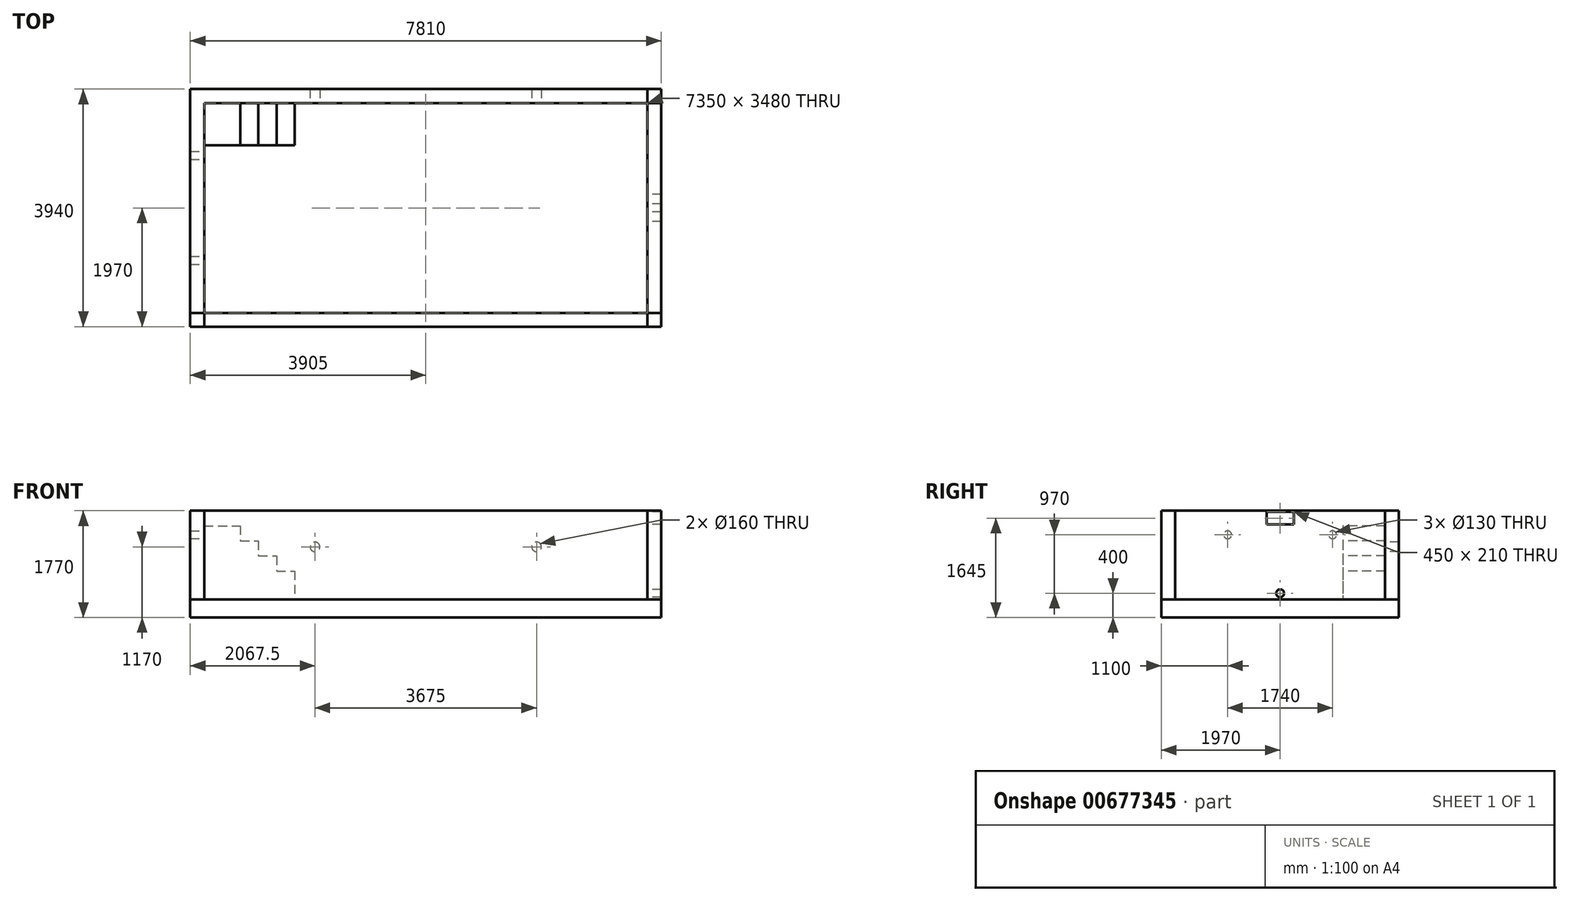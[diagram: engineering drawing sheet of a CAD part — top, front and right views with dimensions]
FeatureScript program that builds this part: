
annotation { "Feature Type Name" : "Feature", "Feature Type Description" : "" }
export const myFeature = defineFeature(function(context is Context, id is Id, definition is map)
    precondition{}
    {
        {
            var Q0;
            Q0=qCreatedBy(makeId("Top.planeOp"),FACE);
            var sketch = newSketch(context, id + "F0", { "sketchPlane" : qUnion([Q0])});
            skLineSegment(sketch, "E0.bottom", {"start": v(-3905, -1970) * mm, "end": v(3905, -1970) * mm});
            skLineSegment(sketch, "E0.top", {"start": v(-3905, 1970) * mm, "end": v(3905, 1970) * mm});
            skLineSegment(sketch, "E0.left", {"start": v(-3905, -1970) * mm, "end": v(-3905, 1970) * mm});
            skLineSegment(sketch, "E0.right", {"start": v(3905, -1970) * mm, "end": v(3905, 1970) * mm});
            skPoint(sketch, "E0.middle", {"position": v(0, 0) * mm});
            skSolve(sketch);
        }
        {
            var Q0;
            Q0=qSketchRegion(id+"F0",true);
            extrude(context, id + "F1", {"entities" : qUnion([Q0]), "oppositeDirection" : true, "depth" : 300 * mm});
        }
        {
            var Q0;
            Q0=makeQuery(id+"F1.opExtrude","CAP_FACE",FACE,{"disambiguationData":[OSD([sQuery(id+"F0.wireOp",EDGE,"E0.bottom"),sQuery(id+"F0.wireOp",EDGE,"E0.top"),sQuery(id+"F0.wireOp",EDGE,"E0.left"),sQuery(id+"F0.wireOp",EDGE,"E0.right")])],"isStart":true});
            var sketch = newSketch(context, id + "F2", { "sketchPlane" : qUnion([Q0])});
            skLineSegment(sketch, "E1.bottom", {"start": v(-3905, 1970) * mm, "end": v(-3675, 1970) * mm});
            skLineSegment(sketch, "E1.top", {"start": v(-3905, -1970) * mm, "end": v(-3675, -1970) * mm});
            skLineSegment(sketch, "E1.left", {"start": v(-3905, 1970) * mm, "end": v(-3905, -1970) * mm});
            skLineSegment(sketch, "E1.right", {"start": v(-3675, 1970) * mm, "end": v(-3675, -1970) * mm});
            skLineSegment(sketch, "E2.bottom", {"start": v(3905, 1970) * mm, "end": v(3675, 1970) * mm});
            skLineSegment(sketch, "E2.top", {"start": v(3905, -1970) * mm, "end": v(3675, -1970) * mm});
            skLineSegment(sketch, "E2.left", {"start": v(3905, 1970) * mm, "end": v(3905, -1970) * mm});
            skLineSegment(sketch, "E2.right", {"start": v(3675, 1970) * mm, "end": v(3675, -1970) * mm});
            skLineSegment(sketch, "E3.bottom", {"start": v(-3675, 1970) * mm, "end": v(3675, 1970) * mm});
            skLineSegment(sketch, "E3.top", {"start": v(-3675, 1740) * mm, "end": v(3675, 1740) * mm});
            skLineSegment(sketch, "E3.left", {"start": v(-3675, 1970) * mm, "end": v(-3675, 1740) * mm});
            skLineSegment(sketch, "E3.right", {"start": v(3675, 1970) * mm, "end": v(3675, 1740) * mm});
            skLineSegment(sketch, "E4.bottom", {"start": v(-3675, -1970) * mm, "end": v(3675, -1970) * mm});
            skLineSegment(sketch, "E4.top", {"start": v(-3675, -1740) * mm, "end": v(3675, -1740) * mm});
            skLineSegment(sketch, "E4.left", {"start": v(-3675, -1970) * mm, "end": v(-3675, -1740) * mm});
            skLineSegment(sketch, "E4.right", {"start": v(3675, -1970) * mm, "end": v(3675, -1740) * mm});
            skLineSegment(sketch, "E5.bottom", {"start": v(-3675, -1740) * mm, "end": v(-3905, -1740) * mm});
            skLineSegment(sketch, "E5.top", {"start": v(-3675, -1970) * mm, "end": v(-3905, -1970) * mm});
            skLineSegment(sketch, "E5.left", {"start": v(-3675, -1740) * mm, "end": v(-3675, -1970) * mm});
            skLineSegment(sketch, "E5.right", {"start": v(-3905, -1740) * mm, "end": v(-3905, -1970) * mm});
            skLineSegment(sketch, "E6.bottom", {"start": v(-3675, 1740) * mm, "end": v(-3905, 1740) * mm});
            skLineSegment(sketch, "E6.top", {"start": v(-3675, 1970) * mm, "end": v(-3905, 1970) * mm});
            skLineSegment(sketch, "E6.left", {"start": v(-3675, 1740) * mm, "end": v(-3675, 1970) * mm});
            skLineSegment(sketch, "E6.right", {"start": v(-3905, 1740) * mm, "end": v(-3905, 1970) * mm});
            skLineSegment(sketch, "E7.bottom", {"start": v(3675, 1740) * mm, "end": v(3905, 1740) * mm});
            skLineSegment(sketch, "E7.top", {"start": v(3675, 1970) * mm, "end": v(3905, 1970) * mm});
            skLineSegment(sketch, "E7.left", {"start": v(3675, 1740) * mm, "end": v(3675, 1970) * mm});
            skLineSegment(sketch, "E7.right", {"start": v(3905, 1740) * mm, "end": v(3905, 1970) * mm});
            skLineSegment(sketch, "E8.bottom", {"start": v(3675, -1740) * mm, "end": v(3905, -1740) * mm});
            skLineSegment(sketch, "E8.top", {"start": v(3675, -1970) * mm, "end": v(3905, -1970) * mm});
            skLineSegment(sketch, "E8.left", {"start": v(3675, -1740) * mm, "end": v(3675, -1970) * mm});
            skLineSegment(sketch, "E8.right", {"start": v(3905, -1740) * mm, "end": v(3905, -1970) * mm});
            skSolve(sketch);
        }
        {
            var Q0;
            Q0=makeQuery(id+"F2.imprint","IMPRINT",FACE,{"disambiguationData":[TD([[makeQuery(id+"F2.imprint","IMPRINT",EDGE,{"derivedFrom":sQuery(id+"F2.wireOp",EDGE,"E1.left")}),-1.0]])]});
            var Q1;
            Q1=makeQuery(id+"F2.imprint","IMPRINT",FACE,{"disambiguationData":[TD([[makeQuery(id+"F2.imprint","IMPRINT",EDGE,{"derivedFrom":sQuery(id+"F2.wireOp",EDGE,"E2.left")}),1.0]])]});
            var Q2;
            Q2=makeQuery(id+"F2.imprint","IMPRINT",FACE,{"disambiguationData":[TD([[makeQuery(id+"F2.imprint","IMPRINT",EDGE,{"derivedFrom":sQuery(id+"F2.wireOp",EDGE,"E3.bottom")}),-1.0]])]});
            var Q3;
            Q3=makeQuery(id+"F2.imprint","IMPRINT",FACE,{"disambiguationData":[TD([[makeQuery(id+"F2.imprint","IMPRINT",EDGE,{"derivedFrom":sQuery(id+"F2.wireOp",EDGE,"E4.bottom")}),1.0]])]});
            extrude(context, id + "F3", {"entities" : qUnion([Q0, Q1, Q2, Q3]), "depth" : 1470 * mm, "offsetDistance" : 25 * mm});
        }
        {
            var Q0;
            Q0=makeQuery(id+"F2.imprint","IMPRINT",FACE,{"disambiguationData":[TD([[makeQuery(id+"F2.imprint","IMPRINT",EDGE,{"derivedFrom":sQuery(id+"F2.wireOp",EDGE,"E5.bottom")}),1.0]])]});
            var Q1;
            Q1=makeQuery(id+"F2.imprint","IMPRINT",FACE,{"disambiguationData":[TD([[makeQuery(id+"F2.imprint","IMPRINT",EDGE,{"derivedFrom":sQuery(id+"F2.wireOp",EDGE,"E6.bottom")}),-1.0]])]});
            var Q2;
            Q2=makeQuery(id+"F2.imprint","IMPRINT",FACE,{"disambiguationData":[TD([[makeQuery(id+"F2.imprint","IMPRINT",EDGE,{"derivedFrom":sQuery(id+"F2.wireOp",EDGE,"E7.bottom")}),1.0]])]});
            var Q3;
            Q3=makeQuery(id+"F2.imprint","IMPRINT",FACE,{"disambiguationData":[TD([[makeQuery(id+"F2.imprint","IMPRINT",EDGE,{"derivedFrom":sQuery(id+"F2.wireOp",EDGE,"E8.bottom")}),-1.0]])]});
            extrude(context, id + "F4", {"entities" : qUnion([Q0, Q1, Q2, Q3]), "depth" : 1470 * mm, "offsetDistance" : 25 * mm});
        }
        {
            var Q0;
            Q0=makeQuery(id+"F1.opExtrude","CAP_FACE",FACE,{"disambiguationData":[OSD([sQuery(id+"F0.wireOp",EDGE,"E0.bottom"),sQuery(id+"F0.wireOp",EDGE,"E0.top"),sQuery(id+"F0.wireOp",EDGE,"E0.left"),sQuery(id+"F0.wireOp",EDGE,"E0.right")])],"isStart":true});
            var sketch = newSketch(context, id + "F5", { "sketchPlane" : qUnion([Q0])});
            skLineSegment(sketch, "E9.bottom", {"start": v(-3905, 1970) * mm, "end": v(-3675, 1970) * mm});
            skLineSegment(sketch, "E9.top", {"start": v(-3905, 1740) * mm, "end": v(-3675, 1740) * mm});
            skLineSegment(sketch, "E9.left", {"start": v(-3905, 1970) * mm, "end": v(-3905, 1740) * mm});
            skLineSegment(sketch, "E9.right", {"start": v(-3675, 1970) * mm, "end": v(-3675, 1740) * mm});
            skLineSegment(sketch, "E10.bottom", {"start": v(-3675, 1740) * mm, "end": v(-2175, 1740) * mm});
            skLineSegment(sketch, "E10.top", {"start": v(-3675, 1040) * mm, "end": v(-2175, 1040) * mm});
            skLineSegment(sketch, "E10.left", {"start": v(-3675, 1740) * mm, "end": v(-3675, 1040) * mm});
            skLineSegment(sketch, "E10.right", {"start": v(-2175, 1740) * mm, "end": v(-2175, 1040) * mm});
            skSolve(sketch);
        }
        {
            var Q0;
            Q0=makeQuery(id+"F5.imprint","IMPRINT",FACE,{"disambiguationData":[TD([[makeQuery(id+"F5.imprint","IMPRINT",EDGE,{"derivedFrom":sQuery(id+"F5.wireOp",EDGE,"E10.bottom")}),-1.0]])]});
            extrude(context, id + "F6", {"entities" : qUnion([Q0]), "depth" : 470 * mm, "offsetDistance" : 25 * mm});
        }
        {
            var Q0;
            Q0=makeQuery(id+"F6.opExtrude","CAP_FACE",FACE,{"disambiguationData":[OSD([sQuery(id+"F5.wireOp",EDGE,"E10.bottom"),sQuery(id+"F5.wireOp",EDGE,"E10.top"),sQuery(id+"F5.wireOp",EDGE,"E10.left"),sQuery(id+"F5.wireOp",EDGE,"E10.right")])],"isStart":false});
            var sketch = newSketch(context, id + "F7", { "sketchPlane" : qUnion([Q0])});
            skLineSegment(sketch, "E11.bottom", {"start": v(-3675, 1740) * mm, "end": v(-2475, 1740) * mm});
            skLineSegment(sketch, "E11.top", {"start": v(-3675, 1040) * mm, "end": v(-2475, 1040) * mm});
            skLineSegment(sketch, "E11.left", {"start": v(-3675, 1740) * mm, "end": v(-3675, 1040) * mm});
            skLineSegment(sketch, "E11.right", {"start": v(-2475, 1740) * mm, "end": v(-2475, 1040) * mm});
            skSolve(sketch);
        }
        {
            var Q0;
            Q0 = qSketchRegion(id + "F7", true);
            extrude(context, id + "F8", {"entities" : qUnion([Q0]), "operationType" : NewBodyOperationType.ADD, "depth" : 250 * mm, "offsetDistance" : 25 * mm});
        }
        {
            var Q0;
            Q0=makeQuery(id+"F8.opExtrude","CAP_FACE",FACE,{"disambiguationData":[OSD([sQuery(id+"F7.wireOp",EDGE,"E11.bottom"),sQuery(id+"F7.wireOp",EDGE,"E11.top"),sQuery(id+"F7.wireOp",EDGE,"E11.left"),sQuery(id+"F7.wireOp",EDGE,"E11.right")])],"isStart":false});
            var sketch = newSketch(context, id + "F9", { "sketchPlane" : qUnion([Q0])});
            skLineSegment(sketch, "E12.bottom", {"start": v(-3675, 1740) * mm, "end": v(-2775, 1740) * mm});
            skLineSegment(sketch, "E12.top", {"start": v(-3675, 1040) * mm, "end": v(-2775, 1040) * mm});
            skLineSegment(sketch, "E12.left", {"start": v(-3675, 1740) * mm, "end": v(-3675, 1040) * mm});
            skLineSegment(sketch, "E12.right", {"start": v(-2775, 1740) * mm, "end": v(-2775, 1040) * mm});
            skSolve(sketch);
        }
        {
            var Q0;
            Q0 = qSketchRegion(id + "F9", true);
            extrude(context, id + "F10", {"entities" : qUnion([Q0]), "operationType" : NewBodyOperationType.ADD, "depth" : 250 * mm, "offsetDistance" : 25 * mm});
        }
        {
            var Q0;
            Q0=makeQuery(id+"F10.opExtrude","CAP_FACE",FACE,{"disambiguationData":[OSD([sQuery(id+"F9.wireOp",EDGE,"E12.bottom"),sQuery(id+"F9.wireOp",EDGE,"E12.top"),sQuery(id+"F9.wireOp",EDGE,"E12.left"),sQuery(id+"F9.wireOp",EDGE,"E12.right")])],"isStart":false});
            var sketch = newSketch(context, id + "F11", { "sketchPlane" : qUnion([Q0])});
            skLineSegment(sketch, "E13.bottom", {"start": v(-3675, 1740) * mm, "end": v(-3075, 1740) * mm});
            skLineSegment(sketch, "E13.top", {"start": v(-3675, 1040) * mm, "end": v(-3075, 1040) * mm});
            skLineSegment(sketch, "E13.left", {"start": v(-3675, 1740) * mm, "end": v(-3675, 1040) * mm});
            skLineSegment(sketch, "E13.right", {"start": v(-3075, 1740) * mm, "end": v(-3075, 1040) * mm});
            skSolve(sketch);
        }
        {
            var Q0;
            Q0 = qSketchRegion(id + "F11", true);
            extrude(context, id + "F12", {"entities" : qUnion([Q0]), "operationType" : NewBodyOperationType.ADD, "depth" : 250 * mm, "offsetDistance" : 25 * mm});
        }
        {
            var Q0;
            Q0=makeQuery(id+"F3.opExtrude","SWEPT_FACE",FACE,{"disambiguationData":[OSD([sQuery(id+"F2.wireOp",EDGE,"E3.top")])]});
            var sketch = newSketch(context, id + "F13", { "sketchPlane" : qUnion([Q0])});
            skLineSegment(sketch, "E14.bottom", {"start": v(-3675, 1470) * mm, "end": v(-1837.5, 1470) * mm});
            skLineSegment(sketch, "E14.top", {"start": v(-3675, 870) * mm, "end": v(-1837.5, 870) * mm});
            skLineSegment(sketch, "E14.left", {"start": v(-3675, 1470) * mm, "end": v(-3675, 870) * mm});
            skLineSegment(sketch, "E14.right", {"start": v(-1837.5, 1470) * mm, "end": v(-1837.5, 870) * mm});
            skLineSegment(sketch, "E15.bottom", {"start": v(3675, 1470) * mm, "end": v(1837.5, 1470) * mm});
            skLineSegment(sketch, "E15.top", {"start": v(3675, 870) * mm, "end": v(1837.5, 870) * mm});
            skLineSegment(sketch, "E15.left", {"start": v(3675, 1470) * mm, "end": v(3675, 870) * mm});
            skLineSegment(sketch, "E15.right", {"start": v(1837.5, 1470) * mm, "end": v(1837.5, 870) * mm});
            skCircle(sketch, "E16", {"center": v(-1837.5, 870) * mm, "radius": 80 * mm});
            skCircle(sketch, "E17", {"center": v(1837.5, 870) * mm, "radius": 80 * mm});
            skSolve(sketch);
        }
        {
            var Q0;
            {var subQ0=sQuery(id+"F13.wireOp",EDGE,"E14.right");var subQ1=sQuery(id+"F13.wireOp",EDGE,"E14.top");var subQ2=makeQuery(id+"F13.imprint","INTERSECT",VERTEX,{"derivedFrom":[subQ1,subQ0]});Q0=makeQuery(id+"F13.imprint","IMPRINT",FACE,{"disambiguationData":[TD([[makeQuery(id+"F13.imprint","IMPRINT",EDGE,{"disambiguationData":[TD([[subQ2,1.0]])],"derivedFrom":subQ1}),1.0]])]});}
            var Q1;
            {var subQ0=sQuery(id+"F13.wireOp",EDGE,"E14.right");var subQ1=sQuery(id+"F13.wireOp",EDGE,"E14.top");var subQ2=makeQuery(id+"F13.imprint","INTERSECT",VERTEX,{"derivedFrom":[subQ1,subQ0]});Q1=makeQuery(id+"F13.imprint","IMPRINT",FACE,{"disambiguationData":[TD([[makeQuery(id+"F13.imprint","IMPRINT",EDGE,{"disambiguationData":[TD([[subQ2,1.0]])],"derivedFrom":subQ1}),-1.0]])]});}
            var Q2;
            {var subQ0=sQuery(id+"F13.wireOp",EDGE,"E15.right");var subQ1=sQuery(id+"F13.wireOp",EDGE,"E15.top");var subQ2=makeQuery(id+"F13.imprint","INTERSECT",VERTEX,{"derivedFrom":[subQ1,subQ0]});Q2=makeQuery(id+"F13.imprint","IMPRINT",FACE,{"disambiguationData":[TD([[makeQuery(id+"F13.imprint","IMPRINT",EDGE,{"disambiguationData":[TD([[subQ2,1.0]])],"derivedFrom":subQ1}),-1.0]])]});}
            var Q3;
            {var subQ0=sQuery(id+"F13.wireOp",EDGE,"E15.right");var subQ1=sQuery(id+"F13.wireOp",EDGE,"E15.top");var subQ2=makeQuery(id+"F13.imprint","INTERSECT",VERTEX,{"derivedFrom":[subQ1,subQ0]});Q3=makeQuery(id+"F13.imprint","IMPRINT",FACE,{"disambiguationData":[TD([[makeQuery(id+"F13.imprint","IMPRINT",EDGE,{"disambiguationData":[TD([[subQ2,1.0]])],"derivedFrom":subQ1}),1.0]])]});}
            extrude(context, id + "F14", {"entities" : qUnion([Q0, Q1, Q2, Q3]), "operationType" : NewBodyOperationType.REMOVE, "oppositeDirection" : true, "depth" : 230 * mm, "offsetDistance" : 25 * mm});
        }
        {
            var Q0;
            Q0=makeQuery(id+"F3.opExtrude","SWEPT_FACE",FACE,{"disambiguationData":[OSD([sQuery(id+"F2.wireOp",EDGE,"E1.right")])]});
            var sketch = newSketch(context, id + "F15", { "sketchPlane" : qUnion([Q0])});
            skLineSegment(sketch, "E18.bottom", {"start": v(-1740, 1470) * mm, "end": v(-870, 1470) * mm});
            skLineSegment(sketch, "E18.top", {"start": v(-1740, 1070) * mm, "end": v(-870, 1070) * mm});
            skLineSegment(sketch, "E18.left", {"start": v(-1740, 1470) * mm, "end": v(-1740, 1070) * mm});
            skLineSegment(sketch, "E18.right", {"start": v(-870, 1470) * mm, "end": v(-870, 1070) * mm});
            skLineSegment(sketch, "E19.bottom", {"start": v(1740, 1470) * mm, "end": v(870, 1470) * mm});
            skLineSegment(sketch, "E19.top", {"start": v(1740, 1070) * mm, "end": v(870, 1070) * mm});
            skLineSegment(sketch, "E19.left", {"start": v(1740, 1470) * mm, "end": v(1740, 1070) * mm});
            skLineSegment(sketch, "E19.right", {"start": v(870, 1470) * mm, "end": v(870, 1070) * mm});
            skCircle(sketch, "E20", {"center": v(-870, 1070) * mm, "radius": 65 * mm});
            skCircle(sketch, "E21", {"center": v(870, 1070) * mm, "radius": 65 * mm});
            skSolve(sketch);
        }
        {
            var Q0;
            {var subQ0=sQuery(id+"F15.wireOp",EDGE,"E18.right");var subQ1=sQuery(id+"F15.wireOp",EDGE,"E18.top");var subQ2=makeQuery(id+"F15.imprint","INTERSECT",VERTEX,{"derivedFrom":[subQ1,subQ0]});Q0=makeQuery(id+"F15.imprint","IMPRINT",FACE,{"disambiguationData":[TD([[makeQuery(id+"F15.imprint","IMPRINT",EDGE,{"disambiguationData":[TD([[subQ2,1.0]])],"derivedFrom":subQ1}),1.0]])]});}
            var Q1;
            {var subQ0=sQuery(id+"F15.wireOp",EDGE,"E18.right");var subQ1=sQuery(id+"F15.wireOp",EDGE,"E18.top");var subQ2=makeQuery(id+"F15.imprint","INTERSECT",VERTEX,{"derivedFrom":[subQ1,subQ0]});Q1=makeQuery(id+"F15.imprint","IMPRINT",FACE,{"disambiguationData":[TD([[makeQuery(id+"F15.imprint","IMPRINT",EDGE,{"disambiguationData":[TD([[subQ2,1.0]])],"derivedFrom":subQ1}),-1.0]])]});}
            var Q2;
            {var subQ0=sQuery(id+"F15.wireOp",EDGE,"E19.right");var subQ1=sQuery(id+"F15.wireOp",EDGE,"E19.top");var subQ2=makeQuery(id+"F15.imprint","INTERSECT",VERTEX,{"derivedFrom":[subQ1,subQ0]});Q2=makeQuery(id+"F15.imprint","IMPRINT",FACE,{"disambiguationData":[TD([[makeQuery(id+"F15.imprint","IMPRINT",EDGE,{"disambiguationData":[TD([[subQ2,1.0]])],"derivedFrom":subQ1}),-1.0]])]});}
            var Q3;
            {var subQ0=sQuery(id+"F15.wireOp",EDGE,"E19.right");var subQ1=sQuery(id+"F15.wireOp",EDGE,"E19.top");var subQ2=makeQuery(id+"F15.imprint","INTERSECT",VERTEX,{"derivedFrom":[subQ1,subQ0]});Q3=makeQuery(id+"F15.imprint","IMPRINT",FACE,{"disambiguationData":[TD([[makeQuery(id+"F15.imprint","IMPRINT",EDGE,{"disambiguationData":[TD([[subQ2,1.0]])],"derivedFrom":subQ1}),1.0]])]});}
            extrude(context, id + "F16", {"entities" : qUnion([Q0, Q1, Q2, Q3]), "operationType" : NewBodyOperationType.REMOVE, "oppositeDirection" : true, "depth" : 230 * mm, "offsetDistance" : 25 * mm});
        }
        {
            var Q0;
            Q0=makeQuery(id+"F3.opExtrude","SWEPT_FACE",FACE,{"disambiguationData":[OSD([sQuery(id+"F2.wireOp",EDGE,"E2.right")])]});
            var sketch = newSketch(context, id + "F17", { "sketchPlane" : qUnion([Q0])});
            skPoint(sketch, "E22.oppositeSnap0", {"position": v(0, 0) * mm});
            skLineSegment(sketch, "E22.bottom", {"start": v(-1740, 0) * mm, "end": v(0, 0) * mm});
            skLineSegment(sketch, "E22.top", {"start": v(-1740, 100) * mm, "end": v(0, 100) * mm});
            skLineSegment(sketch, "E22.left", {"start": v(-1740, 0) * mm, "end": v(-1740, 100) * mm});
            skLineSegment(sketch, "E22.right", {"start": v(0, 0) * mm, "end": v(0, 100) * mm});
            skCircle(sketch, "E23", {"center": v(0, 100) * mm, "radius": 65 * mm});
            skPoint(sketch, "E24.oppositeSnap0", {"position": v(0, 1470) * mm});
            skLineSegment(sketch, "E24.bottom", {"start": v(-1740, 1470) * mm, "end": v(0, 1470) * mm});
            skLineSegment(sketch, "E24.top", {"start": v(-1740, 1345) * mm, "end": v(0, 1345) * mm});
            skLineSegment(sketch, "E24.left", {"start": v(-1740, 1470) * mm, "end": v(-1740, 1345) * mm});
            skLineSegment(sketch, "E24.right", {"start": v(0, 1470) * mm, "end": v(0, 1345) * mm});
            skLineSegment(sketch, "E25.bottom", {"start": v(225, 1240) * mm, "end": v(-225, 1240) * mm});
            skLineSegment(sketch, "E25.top", {"start": v(225, 1450) * mm, "end": v(-225, 1450) * mm});
            skLineSegment(sketch, "E25.left", {"start": v(225, 1240) * mm, "end": v(225, 1450) * mm});
            skLineSegment(sketch, "E25.right", {"start": v(-225, 1240) * mm, "end": v(-225, 1450) * mm});
            skPoint(sketch, "E25.middle", {"position": v(0, 1345) * mm});
            skSolve(sketch);
        }
        {
            var Q0;
            {var subQ0=sQuery(id+"F17.wireOp",EDGE,"E22.right");var subQ1=sQuery(id+"F17.wireOp",EDGE,"E22.top");var subQ2=makeQuery(id+"F17.imprint","INTERSECT",VERTEX,{"derivedFrom":[subQ1,subQ0]});Q0=makeQuery(id+"F17.imprint","IMPRINT",FACE,{"disambiguationData":[TD([[makeQuery(id+"F17.imprint","IMPRINT",EDGE,{"disambiguationData":[TD([[subQ2,1.0]])],"derivedFrom":subQ1}),-1.0]])]});}
            var Q1;
            {var subQ0=sQuery(id+"F17.wireOp",EDGE,"E22.right");var subQ1=sQuery(id+"F17.wireOp",EDGE,"E22.top");var subQ2=makeQuery(id+"F17.imprint","INTERSECT",VERTEX,{"derivedFrom":[subQ1,subQ0]});Q1=makeQuery(id+"F17.imprint","IMPRINT",FACE,{"disambiguationData":[TD([[makeQuery(id+"F17.imprint","IMPRINT",EDGE,{"disambiguationData":[TD([[subQ2,1.0]])],"derivedFrom":subQ1}),1.0]])]});}
            var Q2;
            {var subQ0=sQuery(id+"F17.wireOp",EDGE,"E25.bottom");Q2=makeQuery(id+"F17.imprint","IMPRINT",FACE,{"disambiguationData":[TD([[makeQuery(id+"F17.imprint","IMPRINT",EDGE,{"derivedFrom":subQ0}),-1.0]])]});}
            var Q3;
            {var subQ0=sQuery(id+"F17.wireOp",EDGE,"E24.right");var subQ1=sQuery(id+"F17.wireOp",EDGE,"E24.top");var subQ2=makeQuery(id+"F17.imprint","INTERSECT",VERTEX,{"derivedFrom":[subQ1,subQ0]});Q3=makeQuery(id+"F17.imprint","IMPRINT",FACE,{"disambiguationData":[TD([[makeQuery(id+"F17.imprint","IMPRINT",EDGE,{"disambiguationData":[TD([[subQ2,1.0]])],"derivedFrom":subQ1}),1.0]])]});}
            extrude(context, id + "F18", {"entities" : qUnion([Q0, Q1, Q2, Q3]), "operationType" : NewBodyOperationType.REMOVE, "oppositeDirection" : true, "depth" : 230 * mm, "offsetDistance" : 25 * mm});
        }
    });
